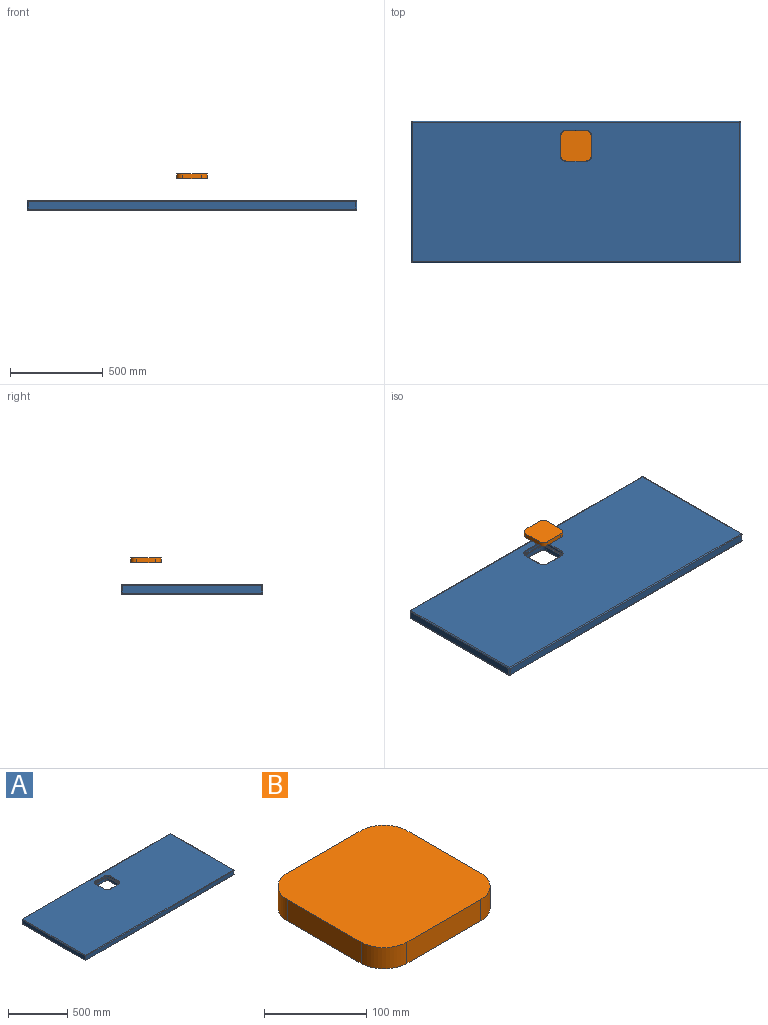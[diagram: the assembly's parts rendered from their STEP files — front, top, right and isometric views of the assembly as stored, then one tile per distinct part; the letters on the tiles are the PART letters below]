
ASSEMBLY  parts=2 mates=1
PART A: 75 faces, bbox 1778x762x50.8 mm
  f0: plane 1767.84x751.84mm, normal (0,0,1), area 1301180.9mm2, adj f17,f18,f27,f28,f43,f44,f45,f46
  f1: plane 101.6x26.67mm, normal (-1,0,0), area 2709.7mm2, adj f2,f8,f62,f71
  f2: cylinder r=25.4mm len=26.67mm, axis (0,0,1), area 1064.1mm2, adj f1,f3,f60,f69
  f3: plane 101.6x26.67mm, normal (0,-1,0), area 2709.7mm2, adj f2,f4,f59,f67
  f4: cylinder r=25.4mm len=26.67mm, axis (0,0,1), area 1064.1mm2, adj f3,f5,f61,f68
  f5: plane 101.6x26.67mm, normal (1,0,0), area 2709.7mm2, adj f4,f6,f63,f70
  f6: cylinder r=25.4mm len=26.67mm, axis (0,0,1), area 1064.1mm2, adj f5,f7,f65,f72
  f7: plane 101.6x26.67mm, normal (0,1,0), area 2709.7mm2, adj f6,f8,f66,f74
  f8: cylinder r=25.4mm len=26.67mm, axis (0,0,1), area 1064.1mm2, adj f1,f7,f64,f73
  f9: plane 1767.84x751.84mm, normal (0,0,-1), area 1305003mm2, adj f20,f21,f29,f30,f67,f68,f69,f70
  f10: plane 751.84x40.64mm, normal (-1,0,0), area 30554.8mm2, adj f22,f27,f30,f33
  f11: plane 1767.84x40.64mm, normal (0,-1,0), area 71845mm2, adj f19,f28,f29,f33
  f12: plane 751.84x40.64mm, normal (1,0,0), area 30554.8mm2, adj f14,f18,f19,f20
  f13: plane 1767.84x40.64mm, normal (0,1,0), area 71845mm2, adj f14,f17,f21,f22
  f14: cylinder r=5.08mm len=40.64mm, axis (0,0,1), area 324.3mm2, adj f12,f13,f15,f16
  f15: sphere r=5.08mm, area 40.5mm2, adj f14,f17,f18
  f16: sphere r=5.08mm, area 40.5mm2, adj f14,f20,f21
  f17: cylinder r=5.08mm len=1767.84mm, axis (1,0,0), area 14106.7mm2, adj f0,f13,f15,f23
  f18: cylinder r=5.08mm len=751.84mm, axis (0,-1,0), area 5999.4mm2, adj f0,f12,f15,f24
  f19: cylinder r=5.08mm len=40.64mm, axis (0,0,-1), area 324.3mm2, adj f11,f12,f24,f25
  f20: cylinder r=5.08mm len=751.84mm, axis (0,1,0), area 5999.4mm2, adj f9,f12,f16,f25
  f21: cylinder r=5.08mm len=1767.84mm, axis (-1,0,0), area 14106.7mm2, adj f9,f13,f16,f26
  f22: cylinder r=5.08mm len=40.64mm, axis (0,0,-1), area 324.3mm2, adj f10,f13,f23,f26
  f23: sphere r=5.08mm, area 40.5mm2, adj f17,f22,f27
  f24: sphere r=5.08mm, area 40.5mm2, adj f18,f19,f28
  f25: sphere r=5.08mm, area 40.5mm2, adj f19,f20,f29
  f26: sphere r=5.08mm, area 40.5mm2, adj f21,f22,f30
  f27: cylinder r=5.08mm len=751.84mm, axis (0,1,0), area 5999.4mm2, adj f0,f10,f23,f31
  f28: cylinder r=5.08mm len=1767.84mm, axis (-1,0,0), area 14106.7mm2, adj f0,f11,f24,f31
  f29: cylinder r=5.08mm len=1767.84mm, axis (1,0,0), area 14106.7mm2, adj f9,f11,f25,f32
  f30: cylinder r=5.08mm len=751.84mm, axis (0,-1,0), area 5999.4mm2, adj f9,f10,f26,f32
  f31: sphere r=5.08mm, area 40.5mm2, adj f27,f28,f33
  f32: sphere r=5.08mm, area 40.5mm2, adj f29,f30,f33
  f33: cylinder r=5.08mm len=40.64mm, axis (0,0,1), area 324.3mm2, adj f10,f11,f31,f32
  f34: plane 101.6x13.97mm, normal (0,-1,0), area 1419.4mm2, adj f35,f41,f43,f51
  f35: cylinder r=31.75mm len=31.75mm, axis (0,0,1), area 696.7mm2, adj f34,f36,f45,f53
  f36: plane 101.6x13.97mm, normal (1,0,0), area 1419.4mm2, adj f35,f37,f47,f55
  f37: cylinder r=31.75mm len=31.75mm, axis (0,0,1), area 696.7mm2, adj f36,f38,f49,f57
  f38: plane 101.6x13.97mm, normal (0,1,0), area 1419.4mm2, adj f37,f39,f50,f58
  f39: cylinder r=31.75mm len=31.75mm, axis (0,0,1), area 696.7mm2, adj f38,f40,f48,f56
  f40: plane 101.6x13.97mm, normal (-1,0,0), area 1419.4mm2, adj f39,f41,f46,f54
  f41: cylinder r=31.75mm len=31.75mm, axis (0,0,1), area 696.7mm2, adj f34,f40,f44,f52
  f42: plane 160.02x160.02mm, normal (0,0,1), area 744.1mm2, adj f51,f52,f53,f54,f55,f56,f57,f58
  f43: cylinder r=2.54mm len=101.6mm, axis (1,0,0), area 405.4mm2, adj f0,f34,f44,f45
  f44: torus R=34.29mm, axis (0,0,1), area 204.8mm2, adj f0,f41,f43,f46
  f45: torus R=34.29mm, axis (0,0,1), area 204.8mm2, adj f0,f35,f43,f47
  f46: cylinder r=2.54mm len=101.6mm, axis (0,-1,0), area 405.4mm2, adj f0,f40,f44,f48
  f47: cylinder r=2.54mm len=101.6mm, axis (0,1,0), area 405.4mm2, adj f0,f36,f45,f49
  f48: torus R=34.29mm, axis (0,0,1), area 204.8mm2, adj f0,f39,f46,f50
  f49: torus R=34.29mm, axis (0,0,1), area 204.8mm2, adj f0,f37,f47,f50
  f50: cylinder r=2.54mm len=101.6mm, axis (-1,0,0), area 405.4mm2, adj f0,f38,f48,f49
  f51: cylinder r=2.54mm len=101.6mm, axis (-1,0,0), area 405.4mm2, adj f34,f42,f52,f53
  f52: torus R=29.21mm, axis (0,0,1), area 193.2mm2, adj f41,f42,f51,f54
  f53: torus R=29.21mm, axis (0,0,1), area 193.2mm2, adj f35,f42,f51,f55
  f54: cylinder r=2.54mm len=101.6mm, axis (0,1,0), area 405.4mm2, adj f40,f42,f52,f56
  f55: cylinder r=2.54mm len=101.6mm, axis (0,-1,0), area 405.4mm2, adj f36,f42,f53,f57
  f56: torus R=29.21mm, axis (0,0,1), area 193.2mm2, adj f39,f42,f54,f58
  f57: torus R=29.21mm, axis (0,0,1), area 193.2mm2, adj f37,f42,f55,f58
  f58: cylinder r=2.54mm len=101.6mm, axis (1,0,0), area 405.4mm2, adj f38,f42,f56,f57
  f59: cylinder r=2.54mm len=101.6mm, axis (1,0,0), area 405.4mm2, adj f3,f42,f60,f61
  f60: torus R=27.94mm, axis (0,0,1), area 165mm2, adj f2,f42,f59,f62
  f61: torus R=27.94mm, axis (0,0,1), area 165mm2, adj f4,f42,f59,f63
  f62: cylinder r=2.54mm len=101.6mm, axis (0,-1,0), area 405.4mm2, adj f1,f42,f60,f64
  f63: cylinder r=2.54mm len=101.6mm, axis (0,1,0), area 405.4mm2, adj f5,f42,f61,f65
  f64: torus R=27.94mm, axis (0,0,1), area 165mm2, adj f8,f42,f62,f66
  f65: torus R=27.94mm, axis (0,0,1), area 165mm2, adj f6,f42,f63,f66
  f66: cylinder r=2.54mm len=101.6mm, axis (-1,0,0), area 405.4mm2, adj f7,f42,f64,f65
  f67: cylinder r=2.54mm len=101.6mm, axis (1,0,0), area 405.4mm2, adj f3,f9,f68,f69
  f68: torus R=27.94mm, axis (0,0,1), area 165mm2, adj f4,f9,f67,f70
  f69: torus R=27.94mm, axis (0,0,1), area 165mm2, adj f2,f9,f67,f71
  f70: cylinder r=2.54mm len=101.6mm, axis (0,1,0), area 405.4mm2, adj f5,f9,f68,f72
  f71: cylinder r=2.54mm len=101.6mm, axis (0,-1,0), area 405.4mm2, adj f1,f9,f69,f73
  f72: torus R=27.94mm, axis (0,0,1), area 165mm2, adj f6,f9,f70,f74
  f73: torus R=27.94mm, axis (0,0,1), area 165mm2, adj f8,f9,f71,f74
  f74: cylinder r=2.54mm len=101.6mm, axis (-1,0,0), area 405.4mm2, adj f7,f9,f72,f73
PART B: 10 faces, bbox 165.1x165.1x25.4 mm
  f0: plane 101.6x25.4mm, normal (1,0,0), area 2580.6mm2, adj f1,f7,f8,f9
  f1: cylinder r=31.75mm len=31.75mm, axis (0,0,-1), area 1266.8mm2, adj f0,f2,f8,f9
  f2: plane 101.6x25.4mm, normal (0,1,0), area 2580.6mm2, adj f1,f3,f8,f9
  f3: cylinder r=31.75mm len=31.75mm, axis (0,0,-1), area 1266.8mm2, adj f2,f4,f8,f9
  f4: plane 101.6x25.4mm, normal (-1,0,0), area 2580.6mm2, adj f3,f5,f8,f9
  f5: cylinder r=31.75mm len=31.75mm, axis (0,0,-1), area 1266.8mm2, adj f4,f6,f8,f9
  f6: plane 101.6x25.4mm, normal (0,-1,0), area 2580.6mm2, adj f5,f7,f8,f9
  f7: cylinder r=31.75mm len=31.75mm, axis (0,0,-1), area 1266.8mm2, adj f0,f6,f8,f9
  f8: plane 165.1x165.1mm, normal (0,0,1), area 26392.7mm2, adj f0,f1,f2,f3,f4,f5,f6,f7
  f9: plane 165.1x165.1mm, normal (0,0,-1), area 26392.7mm2, adj f0,f1,f2,f3,f4,f5,f6,f7
PLACE A t=(-233.71,84.44,1.77)mm
PLACE B t=(655.29,714.36,171.64)mm
MATE slider B.f5 <-> A.f6  axis (0,0,-1) through (604.49,663.56,184.34)mm
